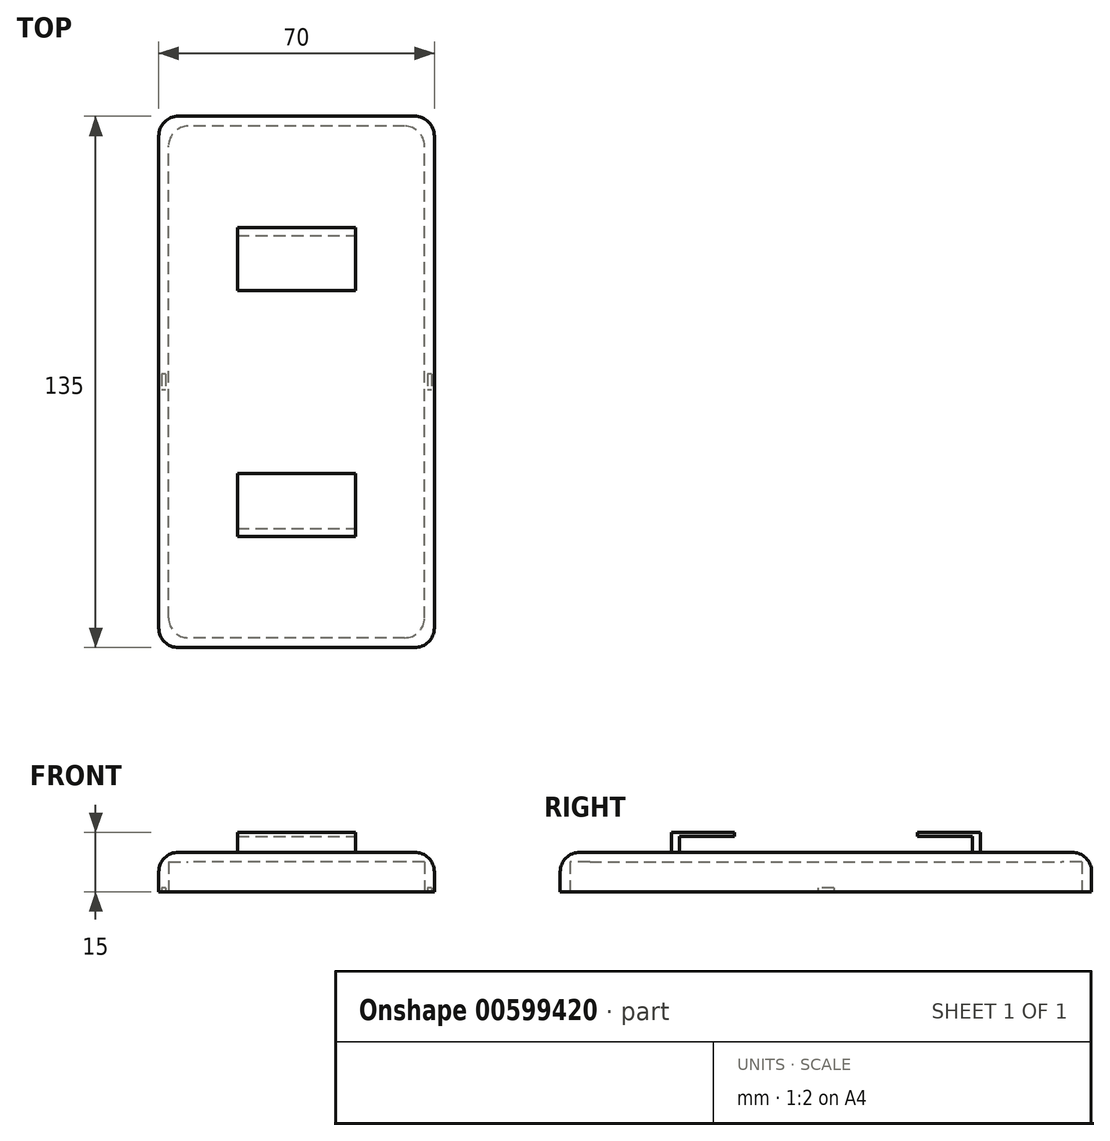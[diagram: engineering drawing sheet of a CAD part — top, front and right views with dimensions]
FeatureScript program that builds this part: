
annotation { "Feature Type Name" : "Feature", "Feature Type Description" : "" }
export const myFeature = defineFeature(function(context is Context, id is Id, definition is map)
    precondition{}
    {
        {
            var Q0;
            Q0=qCreatedBy(makeId("Top.planeOp"),FACE);
            var sketch = newSketch(context, id + "F0", { "sketchPlane" : qUnion([Q0])});
            skLineSegment(sketch, "E0.bottom", {"start": v(35, -67.5) * mm, "end": v(-35, -67.5) * mm});
            skLineSegment(sketch, "E0.top", {"start": v(35, 67.5) * mm, "end": v(-35, 67.5) * mm});
            skLineSegment(sketch, "E0.left", {"start": v(35, -67.5) * mm, "end": v(35, 67.5) * mm});
            skLineSegment(sketch, "E0.right", {"start": v(-35, -67.5) * mm, "end": v(-35, 67.5) * mm});
            skPoint(sketch, "E0.middle", {"position": v(0, 0) * mm});
            skSolve(sketch);
        }
        {
            var Q0;
            Q0=makeQuery(id+"F0.imprint","IMPRINT",FACE,{"disambiguationData":[TD([[makeQuery(id+"F0.imprint","IMPRINT",EDGE,{"derivedFrom":sQuery(id+"F0.wireOp",EDGE,"E0.bottom")}),-1.0]])]});
            extrude(context, id + "F1", {"entities" : qUnion([Q0]), "depth" : 10 * mm, "offsetDistance" : 25 * mm});
        }
        {
            var Q0;
            Q0=makeQuery(id+"F1.opExtrude","CAP_FACE",FACE,{"disambiguationData":[OSD([sQuery(id+"F0.wireOp",EDGE,"E0.bottom"),sQuery(id+"F0.wireOp",EDGE,"E0.top"),sQuery(id+"F0.wireOp",EDGE,"E0.left"),sQuery(id+"F0.wireOp",EDGE,"E0.right")])],"isStart":true});
            var Q1;
            Q1=makeQuery(id+"F1.opExtrude","SWEPT_BODY",BODY,{"disambiguationData":[OSD([sQuery(id+"F0.wireOp",EDGE,"E0.bottom"),sQuery(id+"F0.wireOp",EDGE,"E0.top"),sQuery(id+"F0.wireOp",EDGE,"E0.left"),sQuery(id+"F0.wireOp",EDGE,"E0.right")])]});
            shell(context, id + "F2", {"entities" : qUnion([Q0]), "parts" : qUnion([Q1]), "thickness" : 2.5 * mm});
        }
        {
            var Q0;
            Q0=makeQuery(id+"F1.opExtrude","CAP_EDGE",EDGE,{"disambiguationData":[OSD([sQuery(id+"F0.wireOp",EDGE,"E0.top")])],"isStart":false});
            var Q1;
            Q1=makeQuery(id+"F1.opExtrude","CAP_EDGE",EDGE,{"disambiguationData":[OSD([sQuery(id+"F0.wireOp",EDGE,"E0.left")])],"isStart":false});
            var Q2;
            Q2=makeQuery(id+"F1.opExtrude","SWEPT_EDGE",EDGE,{"disambiguationData":[OSD([sQuery(id+"F0.wireOp",EDGE,"E0.top"),sQuery(id+"F0.wireOp",EDGE,"E0.left")])]});
            fillet(context, id + "F3", {"entities" : qUnion([Q0, Q1, Q2]), "radius" : 5 * mm, "tangentPropagation" : true, "allowEdgeOverflow" : false});
        }
        {
            var Q0;
            Q0=makeQuery(id+"F3.opFillet","BLEND_EDGE",EDGE,{"blendedFrom":[makeQuery(id+"F1.opExtrude","CAP_EDGE",EDGE,{"disambiguationData":[OSD([sQuery(id+"F0.wireOp",EDGE,"E0.left")])],"isStart":false}),makeQuery(id+"F1.opExtrude","SWEPT_FACE",FACE,{"disambiguationData":[OSD([sQuery(id+"F0.wireOp",EDGE,"E0.bottom")])]})],"blendedInto":[makeQuery(id+"F1.opExtrude","SWEPT_FACE",FACE,{"disambiguationData":[OSD([sQuery(id+"F0.wireOp",EDGE,"E0.bottom")])]})]});
            var Q1;
            Q1=makeQuery(id+"F1.opExtrude","CAP_EDGE",EDGE,{"disambiguationData":[OSD([sQuery(id+"F0.wireOp",EDGE,"E0.bottom")])],"isStart":false});
            fillet(context, id + "F4", {"entities" : qUnion([Q0, Q1]), "radius" : 5 * mm, "tangentPropagation" : true, "allowEdgeOverflow" : false});
        }
        {
            var Q0;
            Q0=makeQuery(id+"F1.opExtrude","CAP_EDGE",EDGE,{"disambiguationData":[OSD([sQuery(id+"F0.wireOp",EDGE,"E0.right")])],"isStart":false});
            var Q1;
            Q1=makeQuery(id+"F4.opFillet","BLEND_EDGE",EDGE,{"blendedFrom":[makeQuery(id+"F1.opExtrude","CAP_EDGE",EDGE,{"disambiguationData":[OSD([sQuery(id+"F0.wireOp",EDGE,"E0.bottom")])],"isStart":false}),makeQuery(id+"F1.opExtrude","SWEPT_FACE",FACE,{"disambiguationData":[OSD([sQuery(id+"F0.wireOp",EDGE,"E0.right")])]})],"blendedInto":[makeQuery(id+"F1.opExtrude","SWEPT_FACE",FACE,{"disambiguationData":[OSD([sQuery(id+"F0.wireOp",EDGE,"E0.right")])]})]});
            fillet(context, id + "F5", {"entities" : qUnion([Q0, Q1]), "radius" : 5 * mm, "tangentPropagation" : true, "allowEdgeOverflow" : false});
        }
        {
            var Q0;
            Q0=makeQuery(id+"F2.opShell","OFFSET_EDGE",EDGE,{"disambiguationData":[OSD([sQuery(id+"F0.wireOp",EDGE,"E0.top"),sQuery(id+"F0.wireOp",EDGE,"E0.left")])]});
            var Q1;
            Q1=makeQuery(id+"F2.opShell","OFFSET_EDGE",EDGE,{"disambiguationData":[OSD([sQuery(id+"F0.wireOp",EDGE,"E0.top"),sQuery(id+"F0.wireOp",EDGE,"E0.right")])]});
            var Q2;
            Q2=makeQuery(id+"F2.opShell","OFFSET_EDGE",EDGE,{"disambiguationData":[OSD([sQuery(id+"F0.wireOp",EDGE,"E0.bottom"),sQuery(id+"F0.wireOp",EDGE,"E0.left")])]});
            var Q3;
            Q3=makeQuery(id+"F2.opShell","OFFSET_EDGE",EDGE,{"disambiguationData":[OSD([sQuery(id+"F0.wireOp",EDGE,"E0.bottom"),sQuery(id+"F0.wireOp",EDGE,"E0.right")])]});
            fillet(context, id + "F6", {"entities" : qUnion([Q0, Q1, Q2, Q3]), "radius" : 5 * mm, "tangentPropagation" : true, "allowEdgeOverflow" : false});
        }
        {
            var Q0;
            Q0=makeQuery(id+"F1.opExtrude","CAP_FACE",FACE,{"disambiguationData":[OSD([sQuery(id+"F0.wireOp",EDGE,"E0.bottom"),sQuery(id+"F0.wireOp",EDGE,"E0.top"),sQuery(id+"F0.wireOp",EDGE,"E0.left"),sQuery(id+"F0.wireOp",EDGE,"E0.right")])],"isStart":true});
            var sketch = newSketch(context, id + "F7", { "sketchPlane" : qUnion([Q0])});
            skLineSegment(sketch, "E1.bottom", {"start": v(34.25, -2) * mm, "end": v(33.25, -2) * mm});
            skLineSegment(sketch, "E1.top", {"start": v(34.25, 2) * mm, "end": v(33.25, 2) * mm});
            skLineSegment(sketch, "E1.left", {"start": v(34.25, -2) * mm, "end": v(34.25, 2) * mm});
            skLineSegment(sketch, "E1.right", {"start": v(33.25, -2) * mm, "end": v(33.25, 2) * mm});
            skPoint(sketch, "E1.middle", {"position": v(33.75, 0) * mm});
            skLineSegment(sketch, "E2.bottom", {"start": v(-33.25, -2) * mm, "end": v(-34.25, -2) * mm});
            skLineSegment(sketch, "E2.top", {"start": v(-33.25, 2) * mm, "end": v(-34.25, 2) * mm});
            skLineSegment(sketch, "E2.left", {"start": v(-33.25, -2) * mm, "end": v(-33.25, 2) * mm});
            skLineSegment(sketch, "E2.right", {"start": v(-34.25, -2) * mm, "end": v(-34.25, 2) * mm});
            skPoint(sketch, "E2.middle", {"position": v(-33.75, 0) * mm});
            skSolve(sketch);
        }
        {
            var Q0;
            Q0=makeQuery(id+"F7.imprint","IMPRINT",FACE,{"disambiguationData":[TD([[makeQuery(id+"F7.imprint","IMPRINT",EDGE,{"derivedFrom":sQuery(id+"F7.wireOp",EDGE,"E2.bottom")}),-1.0]])]});
            var Q1;
            Q1=makeQuery(id+"F7.imprint","IMPRINT",FACE,{"disambiguationData":[TD([[makeQuery(id+"F7.imprint","IMPRINT",EDGE,{"derivedFrom":sQuery(id+"F7.wireOp",EDGE,"E1.bottom")}),-1.0]])]});
            extrude(context, id + "F8", {"entities" : qUnion([Q0, Q1]), "operationType" : NewBodyOperationType.REMOVE, "oppositeDirection" : true, "depth" : 1 * mm, "offsetDistance" : 25 * mm});
        }
        {
            var Q0;
            Q0=makeQuery(id+"F1.opExtrude","CAP_FACE",FACE,{"disambiguationData":[OSD([sQuery(id+"F0.wireOp",EDGE,"E0.bottom"),sQuery(id+"F0.wireOp",EDGE,"E0.top"),sQuery(id+"F0.wireOp",EDGE,"E0.left"),sQuery(id+"F0.wireOp",EDGE,"E0.right")])],"isStart":false});
            var sketch = newSketch(context, id + "F9", { "sketchPlane" : qUnion([Q0])});
            skPoint(sketch, "E3.middle", {"position": v(0, -31.25) * mm});
            skLineSegment(sketch, "E4.bottom", {"start": v(15, 39.25) * mm, "end": v(-15, 39.25) * mm});
            skLineSegment(sketch, "E4.top", {"start": v(15, 23.25) * mm, "end": v(-15, 23.25) * mm});
            skPoint(sketch, "E4.middle", {"position": v(0, 31.25) * mm});
            skLineSegment(sketch, "E5", {"start": v(-15, -23.25) * mm, "end": v(15, -23.25) * mm});
            skLineSegment(sketch, "E6", {"start": v(-15, -37.25) * mm, "end": v(15, -37.25) * mm});
            skLineSegment(sketch, "E7", {"start": v(-15, 37.25) * mm, "end": v(15, 37.25) * mm});
            skPoint(sketch, "E8.start.orphan", {"position": v(15, -31.25) * mm});
            skLineSegment(sketch, "E9.left", {"start": v(15, 39.25) * mm, "end": v(15, 23.25) * mm});
            skLineSegment(sketch, "E9.right", {"start": v(-15, 39.25) * mm, "end": v(-15, 23.25) * mm});
            skPoint(sketch, "E10.orphan", {"position": v(15, 37.25) * mm});
            skPoint(sketch, "E11.orphan", {"position": v(15, 39.25) * mm});
            skPoint(sketch, "E12.orphan", {"position": v(15, 23.25) * mm});
            skPoint(sketch, "E13.orphan", {"position": v(-15, 23.25) * mm});
            skPoint(sketch, "E4.right.start.orphan", {"position": v(-15, 39.25) * mm});
            skLineSegment(sketch, "E14", {"start": v(0, 23.25) * mm, "end": v(15, 23.25) * mm});
            skLineSegment(sketch, "E15.bottom", {"start": v(15, -23.25) * mm, "end": v(-15, -23.25) * mm});
            skLineSegment(sketch, "E15.top", {"start": v(15, -39.25) * mm, "end": v(15, -39.25) * mm});
            skLineSegment(sketch, "E15.left", {"start": v(15, -23.25) * mm, "end": v(15, -39.25) * mm});
            skLineSegment(sketch, "E15.right", {"start": v(-15, -23.25) * mm, "end": v(-15, -39.25) * mm});
            skPoint(sketch, "E16.orphan", {"position": v(15, -39.25) * mm});
            skPoint(sketch, "E17.orphan", {"position": v(15, -23.25) * mm});
            skPoint(sketch, "E18.start.orphan", {"position": v(-15, -39.25) * mm});
            skPoint(sketch, "E19.orphan", {"position": v(-15, -23.25) * mm});
            skLineSegment(sketch, "E20", {"start": v(0, -23.25) * mm, "end": v(15, -23.25) * mm});
            skLineSegment(sketch, "E21", {"start": v(0, -23.25) * mm, "end": v(-15, -23.25) * mm});
            skLineSegment(sketch, "E22", {"start": v(0, -23.25) * mm, "end": v(0, -39.25) * mm});
            skLineSegment(sketch, "E23", {"start": v(0, -39.25) * mm, "end": v(-15, -39.25) * mm});
            skLineSegment(sketch, "E24", {"start": v(0, -39.25) * mm, "end": v(15, -39.25) * mm});
            skPoint(sketch, "E25.start.orphan", {"position": v(-30, 31.25) * mm});
            skPoint(sketch, "E26.end.orphan", {"position": v(30, 31.25) * mm});
            skPoint(sketch, "E26.start.orphan", {"position": v(15, 31.25) * mm});
            skPoint(sketch, "E27.end.orphan", {"position": v(30, -31.25) * mm});
            skPoint(sketch, "E28.end.orphan", {"position": v(-30, -31.25) * mm});
            skPoint(sketch, "E28.start.orphan", {"position": v(-15, -31.25) * mm});
            skPoint(sketch, "E29.start.orphan", {"position": v(0, 0) * mm});
            skPoint(sketch, "E30.start.orphan", {"position": v(0, -62.5) * mm});
            skPoint(sketch, "E31.start.orphan", {"position": v(0, 62.5) * mm});
            skSolve(sketch);
        }
        {
            var Q0;
            {var subQ1=sQuery(id+"F9.wireOp",EDGE,"E7");Q0=makeQuery(id+"F9.imprint","IMPRINT",FACE,{"disambiguationData":[TD([[makeQuery(id+"F9.imprint","IMPRINT",EDGE,{"derivedFrom":subQ1}),1.0]])]});}
            var Q1;
            {var subQ5=sQuery(id+"F9.wireOp",EDGE,"E23");Q1=makeQuery(id+"F9.imprint","IMPRINT",FACE,{"disambiguationData":[TD([[makeQuery(id+"F9.imprint","IMPRINT",EDGE,{"derivedFrom":subQ5}),-1.0]])]});}
            var Q2;
            {var subQ5=sQuery(id+"F9.wireOp",EDGE,"E24");Q2=makeQuery(id+"F9.imprint","IMPRINT",FACE,{"disambiguationData":[TD([[makeQuery(id+"F9.imprint","IMPRINT",EDGE,{"derivedFrom":subQ5}),1.0]])]});}
            extrude(context, id + "F10", {"entities" : qUnion([Q0, Q1, Q2]), "operationType" : NewBodyOperationType.ADD, "depth" : 4 * mm, "offsetDistance" : 25 * mm});
        }
        {
            var Q0;
            Q0=makeQuery(id+"F10.opExtrude","CAP_FACE",FACE,{"disambiguationData":[OSD([sQuery(id+"F9.wireOp",EDGE,"E7"),sQuery(id+"F9.wireOp",EDGE,"E4.bottom"),sQuery(id+"F9.wireOp",EDGE,"E9.left"),sQuery(id+"F9.wireOp",EDGE,"E9.right")])],"isStart":false});
            var sketch = newSketch(context, id + "F11", { "sketchPlane" : qUnion([Q0])});
            skLineSegment(sketch, "E32.bottom", {"start": v(15, 39.25) * mm, "end": v(-15, 39.25) * mm});
            skLineSegment(sketch, "E32.top", {"start": v(15, 23.25) * mm, "end": v(-15, 23.25) * mm});
            skLineSegment(sketch, "E32.left", {"start": v(15, 39.25) * mm, "end": v(15, 23.25) * mm});
            skLineSegment(sketch, "E32.right", {"start": v(-15, 39.25) * mm, "end": v(-15, 23.25) * mm});
            skSolve(sketch);
        }
        {
            var Q0;
            Q0=makeQuery(id+"F10.opExtrude","CAP_FACE",FACE,{"disambiguationData":[OSD([sQuery(id+"F9.wireOp",EDGE,"E6"),sQuery(id+"F9.wireOp",EDGE,"E15.left"),sQuery(id+"F9.wireOp",EDGE,"E15.right"),sQuery(id+"F9.wireOp",EDGE,"E23"),sQuery(id+"F9.wireOp",EDGE,"E24")])],"isStart":false});
            var sketch = newSketch(context, id + "F12", { "sketchPlane" : qUnion([Q0])});
            skLineSegment(sketch, "E33.bottom", {"start": v(15, -39.25) * mm, "end": v(-15, -39.25) * mm});
            skLineSegment(sketch, "E33.top", {"start": v(15, -23.25) * mm, "end": v(-15, -23.25) * mm});
            skLineSegment(sketch, "E33.left", {"start": v(15, -39.25) * mm, "end": v(15, -23.25) * mm});
            skLineSegment(sketch, "E33.right", {"start": v(-15, -39.25) * mm, "end": v(-15, -23.25) * mm});
            skSolve(sketch);
        }
        {
            var Q0;
            {var subQ0=sQuery(id+"F12.wireOp",EDGE,"E33.top");Q0=makeQuery(id+"F12.imprint","IMPRINT",FACE,{"disambiguationData":[TD([[makeQuery(id+"F12.imprint","IMPRINT",EDGE,{"derivedFrom":subQ0}),1.0]])]});}
            var Q1;
            {var subQ0=sQuery(id+"F12.wireOp",EDGE,"E33.bottom");Q1=makeQuery(id+"F12.imprint","IMPRINT",FACE,{"disambiguationData":[TD([[makeQuery(id+"F12.imprint","IMPRINT",EDGE,{"derivedFrom":subQ0}),-1.0]])]});}
            extrude(context, id + "F13", {"entities" : qUnion([Q0, Q1]), "operationType" : NewBodyOperationType.ADD, "depth" : 1 * mm, "offsetDistance" : 25 * mm});
        }
        {
            var Q0;
            {var subQ0=sQuery(id+"F11.wireOp",EDGE,"E32.bottom");Q0=makeQuery(id+"F11.imprint","IMPRINT",FACE,{"disambiguationData":[TD([[makeQuery(id+"F11.imprint","IMPRINT",EDGE,{"derivedFrom":subQ0}),1.0]])]});}
            var Q1;
            {var subQ0=sQuery(id+"F11.wireOp",EDGE,"E32.top");Q1=makeQuery(id+"F11.imprint","IMPRINT",FACE,{"disambiguationData":[TD([[makeQuery(id+"F11.imprint","IMPRINT",EDGE,{"derivedFrom":subQ0}),-1.0]])]});}
            extrude(context, id + "F14", {"entities" : qUnion([Q0, Q1]), "operationType" : NewBodyOperationType.ADD, "depth" : 1 * mm, "offsetDistance" : 25 * mm});
        }
    });
